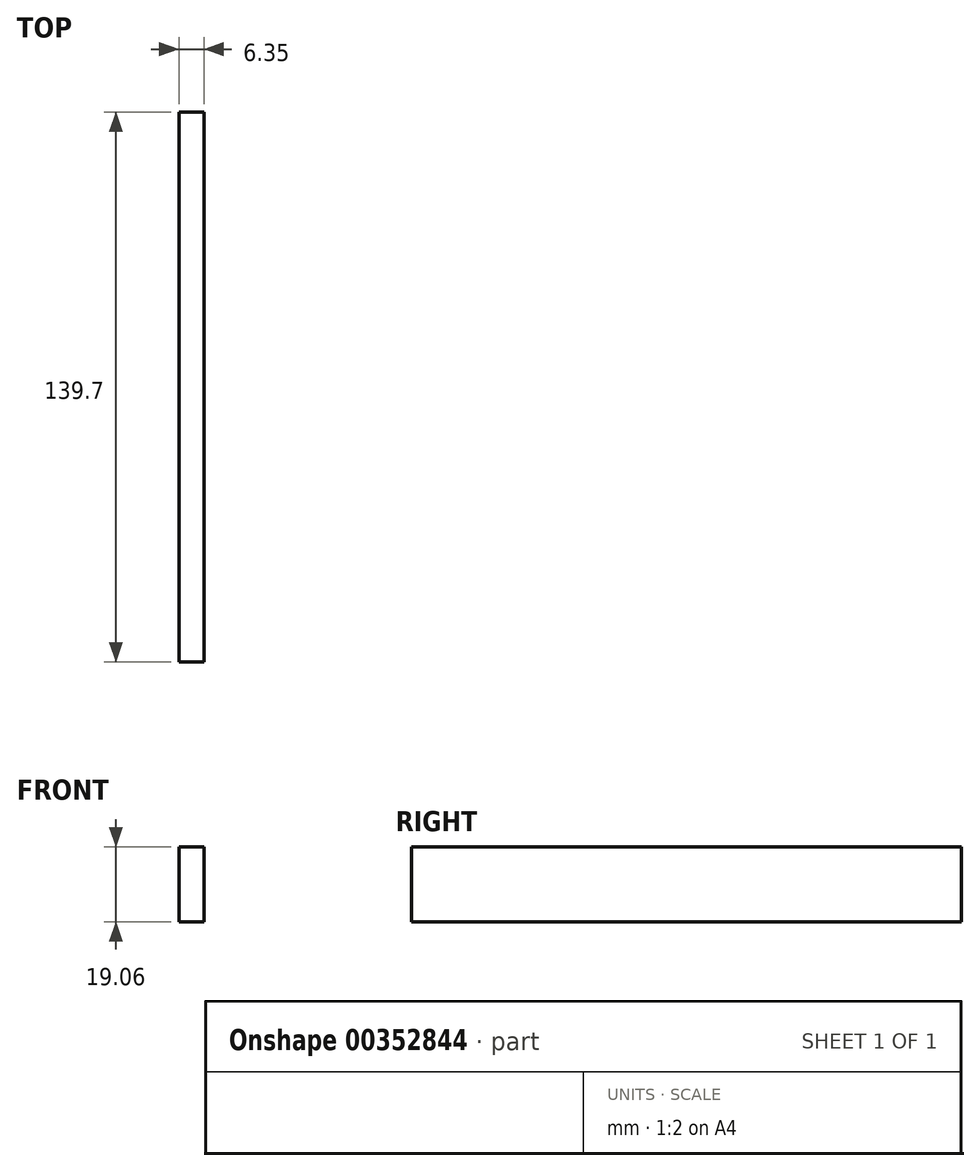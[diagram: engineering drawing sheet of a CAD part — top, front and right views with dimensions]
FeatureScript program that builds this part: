
annotation { "Feature Type Name" : "Feature", "Feature Type Description" : "" }
export const myFeature = defineFeature(function(context is Context, id is Id, definition is map)
    precondition{}
    {
        {
            var Q0;
            Q0=qCreatedBy(makeId("Right.planeOp"),FACE);
            var sketch = newSketch(context, id + "F0", { "sketchPlane" : qUnion([Q0])});
            skLineSegment(sketch, "E0.bottom", {"start": v(69.85, 9.53) * mm, "end": v(-69.85, 9.53) * mm});
            skLineSegment(sketch, "E0.top", {"start": v(69.85, -9.53) * mm, "end": v(-69.85, -9.53) * mm});
            skLineSegment(sketch, "E0.left", {"start": v(69.85, 9.53) * mm, "end": v(69.85, -9.52) * mm});
            skLineSegment(sketch, "E0.right", {"start": v(-69.85, 9.53) * mm, "end": v(-69.85, -9.52) * mm});
            skPoint(sketch, "E0.middle", {"position": v(0, 0) * mm});
            skSolve(sketch);
        }
        {
            var Q0;
            Q0 = qSketchRegion(id + "F0", true);
            extrude(context, id + "F1", {"entities" : qUnion([Q0]), "depth" : 6.35 * mm});
        }
    });
